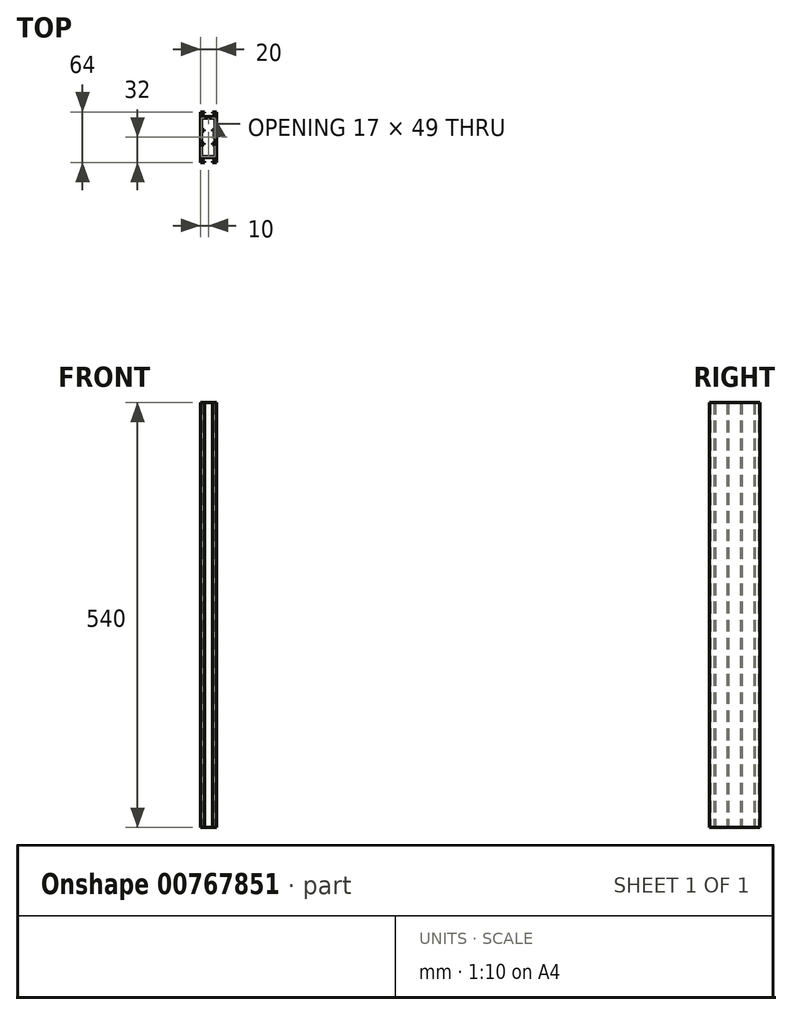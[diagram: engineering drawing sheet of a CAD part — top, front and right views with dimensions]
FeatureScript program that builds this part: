
annotation { "Feature Type Name" : "Feature", "Feature Type Description" : "" }
export const myFeature = defineFeature(function(context is Context, id is Id, definition is map)
    precondition{}
    {
        {
            var Q0;
            Q0=qCreatedBy(makeId("Top.planeOp"),FACE);
            var sketch = newSketch(context, id + "F0", { "sketchPlane" : qUnion([Q0])});
            skLineSegment(sketch, "E0", {"start": v(-5, 32) * mm, "end": v(-10, 32) * mm});
            skLineSegment(sketch, "E1", {"start": v(-10, 32) * mm, "end": v(-10, -32) * mm});
            skLineSegment(sketch, "E2", {"start": v(-10, -32) * mm, "end": v(-5, -32) * mm});
            skLineSegment(sketch, "E3", {"start": v(-5, -32) * mm, "end": v(-5, -30.5) * mm});
            skLineSegment(sketch, "E4", {"start": v(-5, -30.5) * mm, "end": v(-8.5, -30.5) * mm});
            skLineSegment(sketch, "E5", {"start": v(-8.5, -30.5) * mm, "end": v(-8.5, -26) * mm});
            skLineSegment(sketch, "E6", {"start": v(-8.5, -26) * mm, "end": v(8.5, -26) * mm});
            skLineSegment(sketch, "E7", {"start": v(8.5, -26) * mm, "end": v(8.5, -30.5) * mm});
            skLineSegment(sketch, "E8", {"start": v(8.5, -30.5) * mm, "end": v(5, -30.5) * mm});
            skLineSegment(sketch, "E9", {"start": v(5, -30.5) * mm, "end": v(5, -32) * mm});
            skLineSegment(sketch, "E10", {"start": v(5, -32) * mm, "end": v(10, -32) * mm});
            skLineSegment(sketch, "E11", {"start": v(10, -32) * mm, "end": v(10, 32) * mm});
            skLineSegment(sketch, "E12", {"start": v(10, 32) * mm, "end": v(5, 32) * mm});
            skLineSegment(sketch, "E13", {"start": v(5, 32) * mm, "end": v(5, 30.5) * mm});
            skLineSegment(sketch, "E14", {"start": v(5, 30.5) * mm, "end": v(8.5, 30.5) * mm});
            skLineSegment(sketch, "E15", {"start": v(8.5, 30.5) * mm, "end": v(8.5, 26) * mm});
            skLineSegment(sketch, "E16", {"start": v(8.5, 26) * mm, "end": v(-8.5, 26) * mm});
            skLineSegment(sketch, "E17", {"start": v(-8.5, 26) * mm, "end": v(-8.5, 30.5) * mm});
            skLineSegment(sketch, "E18", {"start": v(-8.5, 30.5) * mm, "end": v(-5, 30.5) * mm});
            skLineSegment(sketch, "E19", {"start": v(-5, 30.5) * mm, "end": v(-5, 32) * mm});
            skLineSegment(sketch, "E20", {"start": v(-8.5, 24.5) * mm, "end": v(-8.5, 9.5) * mm});
            skLineSegment(sketch, "E21", {"start": v(-8.5, 9.5) * mm, "end": v(-5.5, 9.5) * mm});
            skLineSegment(sketch, "E22", {"start": v(-5.5, 9.5) * mm, "end": v(-5.5, 7.5) * mm});
            skLineSegment(sketch, "E23", {"start": v(-5.5, 7.5) * mm, "end": v(-8.5, 7.5) * mm});
            skLineSegment(sketch, "E24", {"start": v(-8.5, 7.5) * mm, "end": v(-8.5, -7.5) * mm});
            skLineSegment(sketch, "E25", {"start": v(-8.5, -7.5) * mm, "end": v(-5.5, -7.5) * mm});
            skLineSegment(sketch, "E26", {"start": v(-5.5, -7.5) * mm, "end": v(-5.5, -9.5) * mm});
            skLineSegment(sketch, "E27", {"start": v(-5.5, -9.5) * mm, "end": v(-8.5, -9.5) * mm});
            skLineSegment(sketch, "E28", {"start": v(-8.5, -9.5) * mm, "end": v(-8.5, -24.5) * mm});
            skLineSegment(sketch, "E29", {"start": v(-8.5, -24.5) * mm, "end": v(8.5, -24.5) * mm});
            skLineSegment(sketch, "E30", {"start": v(8.5, -24.5) * mm, "end": v(8.5, -9.5) * mm});
            skLineSegment(sketch, "E31", {"start": v(8.5, -9.5) * mm, "end": v(5.5, -9.5) * mm});
            skLineSegment(sketch, "E32", {"start": v(5.5, -9.5) * mm, "end": v(5.5, -7.5) * mm});
            skLineSegment(sketch, "E33", {"start": v(5.5, -7.5) * mm, "end": v(8.5, -7.5) * mm});
            skLineSegment(sketch, "E34", {"start": v(8.5, -7.5) * mm, "end": v(8.5, 7.5) * mm});
            skLineSegment(sketch, "E35", {"start": v(8.5, 7.5) * mm, "end": v(5.5, 7.5) * mm});
            skLineSegment(sketch, "E36", {"start": v(5.5, 7.5) * mm, "end": v(5.5, 9.5) * mm});
            skLineSegment(sketch, "E37", {"start": v(5.5, 9.5) * mm, "end": v(8.5, 9.5) * mm});
            skLineSegment(sketch, "E38", {"start": v(8.5, 9.5) * mm, "end": v(8.5, 24.5) * mm});
            skLineSegment(sketch, "E39", {"start": v(8.5, 24.5) * mm, "end": v(-8.5, 24.5) * mm});
            skLineSegment(sketch, "E40", {"start": v(0, 26) * mm, "end": v(0, -26) * mm, "construction": true});
            skSolve(sketch);
        }
        {
            var Q0;
            Q0=makeQuery(id+"F0.imprint","IMPRINT",FACE,{"disambiguationData":[TD([[makeQuery(id+"F0.imprint","IMPRINT",EDGE,{"derivedFrom":sQuery(id+"F0.wireOp",EDGE,"E0")}),1.0]])]});
            extrude(context, id + "F1", {"entities" : qUnion([Q0]), "flatOperationType" : FlatOperationType.REMOVE, "depth" : 540 * mm, "offsetDistance" : 25 * mm, "domain" : OperationDomain.MODEL});
        }
    });
